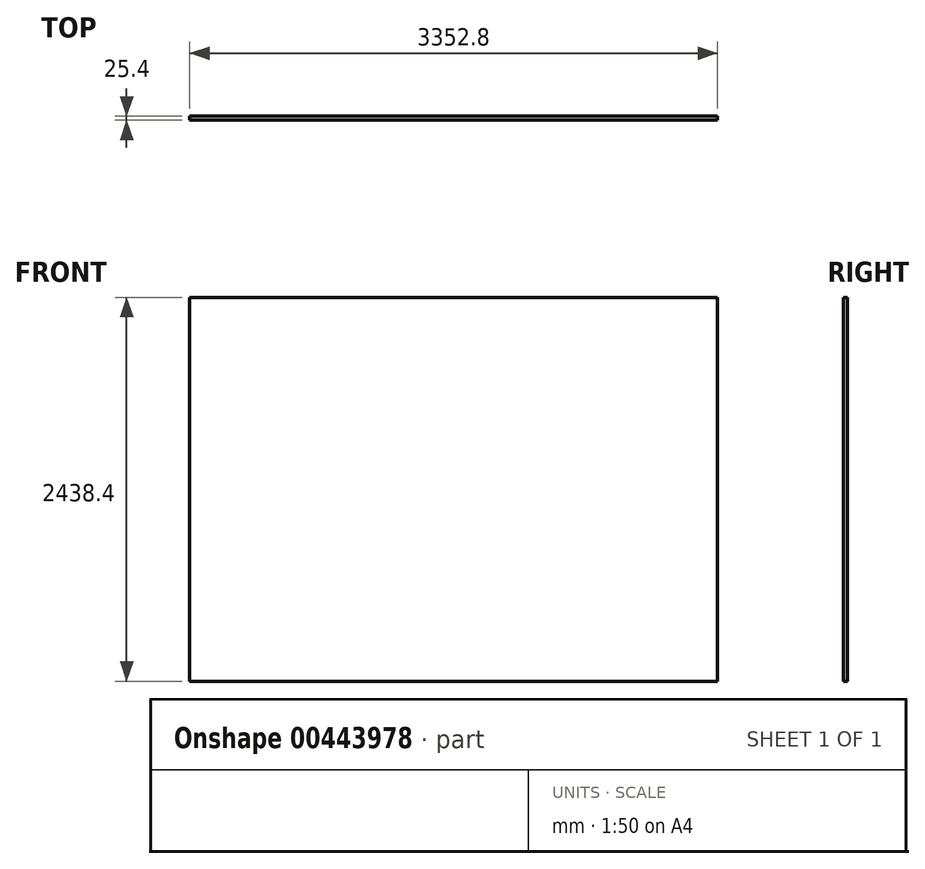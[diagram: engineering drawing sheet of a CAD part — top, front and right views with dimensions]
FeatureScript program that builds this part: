
annotation { "Feature Type Name" : "Feature", "Feature Type Description" : "" }
export const myFeature = defineFeature(function(context is Context, id is Id, definition is map)
    precondition{}
    {
        {
            var Q0;
            Q0=qCreatedBy(makeId("Front.planeOp"),FACE);
            var sketch = newSketch(context, id + "F0", { "sketchPlane" : qUnion([Q0])});
            skLineSegment(sketch, "E0.bottom", {"start": v(1676.4, -1219.2) * mm, "end": v(-1676.4, -1219.2) * mm});
            skLineSegment(sketch, "E0.top", {"start": v(1676.4, 1219.2) * mm, "end": v(-1676.4, 1219.2) * mm});
            skLineSegment(sketch, "E0.left", {"start": v(1676.4, -1219.2) * mm, "end": v(1676.4, 1219.2) * mm});
            skLineSegment(sketch, "E0.right", {"start": v(-1676.4, -1219.2) * mm, "end": v(-1676.4, 1219.2) * mm});
            skPoint(sketch, "E0.middle", {"position": v(0, 0) * mm});
            skSolve(sketch);
        }
        {
            var Q0;
            Q0 = qSketchRegion(id + "F0", true);
            extrude(context, id + "F1", {"entities" : qUnion([Q0]), "depth" : 25.4 * mm});
        }
    });
